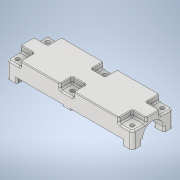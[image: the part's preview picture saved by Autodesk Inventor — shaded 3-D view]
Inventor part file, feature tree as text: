
AUTODESK INVENTOR PART (.ipt)
format: ipt  version: 2020 (Build 240168000, 168)  size: 884,736 bytes
history: native  units: mm
features: sketch x16, extrude x15, projected_geometry x10, other x4, fillet x3, boolean_combine x2, mirror x1
ambient origin geometry x8: Origin, YZ Plane, XZ Plane, XY Plane, X Axis, Y Axis, Z Axis, Center Point
bodies: Volumenkörper1 (feature_tree), Solid2 (feature_tree), Solid3 (feature_tree), Solid4 (feature_tree)
feature tree (51):
  other  "rolinho.ipt"
  extrude  "Extrusion1"  Depth=11.0mm
  other  "Spirale1"
  mirror  "Spiegeln1"
  extrude  "Extrusion5"  Depth=7.0mm
  extrude  "Extrusion6"  Depth=1.0mm
  boolean_combine  "Combine1"
  extrude  "Extrusion7"  Depth=10.0mm TaperAngle=0.0deg
  extrude  "Extrusion8"  Depth=7.0mm TaperAngle=0.0deg
  extrude  "Extrusion9"  Depth=24.0mm
  extrude  "Extrusion10"  Depth=12.0mm TaperAngle=0.0deg
  extrude  "Extrusion11"  Depth=4.0mm
  extrude  "Extrusion13"  Depth=20.0mm
  fillet  "Fillet2"  Radius=10.0mm
  fillet  "Fillet3"  Radius=77.15mm
  fillet  "Fillet4"  Radius=30.0mm
  extrude  "Extrusion14"  Depth=6.0mm
  extrude  "Extrusion15"  Depth=10.0mm TaperAngle=0.0deg
  extrude  "Extrusion16"  Depth=3.0mm
  extrude  "Extrusion17"  Depth=48.0mm
  extrude  "Extrusion19"  Depth=4.0mm
  extrude  "Extrusion20"  Depth=7.9mm
  boolean_combine  "Combine2"
  sketch  "Skizze1"  dims[d0=6.0mm d1=11.0mm]
  sketch  "Skizze3"  dims[d2=36.0mm d3=0.0mm]
  projected_geometry  "Projizierte Kontur2"
  sketch  "Sketch7"  dims[d8=7.0mm d9=24.5mm d10=10.0mm d11=0.0mm d12=90.0deg d13=90.0deg d14=0.0mm d15=0.0mm d16=4.0mm]
  sketch  "Sketch8"  dims[d17=13.962634mm d18=1.0mm]
  sketch  "Sketch9"  dims[d19=0.1mm d32=10.0mm d33=0.0mm]
  projected_geometry  "Projected Loop4"
  sketch  "Sketch10"  dims[d34=7.0mm d35=100.0mm d36=0.0mm]
  sketch  "Sketch11"  dims[d37=82.0mm d38=0.0mm d39=24.0mm]
  projected_geometry  "Projected Loop5"
  projected_geometry  "Projected Loop6"
  sketch  "Sketch12"  dims[d40=30.0mm d41=12.0mm d42=0.0mm]
  sketch  "Sketch13"  dims[d43=3.0mm d44=4.0mm]
  projected_geometry  "Projected Loop7"
  projected_geometry  "Projected Loop8"
  sketch  "Sketch15"  dims[d45=4.0mm d46=20.0mm d48=22.0mm d49=20.0mm d51=84.0mm d54=10.0mm d55=0.0mm d56=77.15mm d57=30.0mm]
  sketch  "Sketch16"  dims[d62=4.0mm d63=0.0mm d64=6.0mm]
  projected_geometry  "Projected Loop10"
  sketch  "Sketch17"  dims[d65=10.0mm d66=0.0mm d67=10.0mm d68=0.0mm]
  projected_geometry  "Projected Loop11"
  projected_geometry  "Projected Loop12"
  sketch  "Sketch18"  dims[d76=3.0mm d77=3.0mm]
  sketch  "Sketch19"  dims[d78=4.0mm d79=48.0mm]
  sketch  "Sketch21"  dims[d80=46.0mm d81=4.0mm]
  projected_geometry  "Projected Loop13"
  sketch  "Sketch22"  dims[d85=7.0mm d86=6.9mm d87=3.5mm d88=7.0mm d89=6.9mm d90=3.5mm d91=10.0mm d92=10.0mm d93=10.0mm d94=10.0mm d95=10.0mm d96=10.0mm d97=10.0mm d98=10.0mm d99=10.0mm d100=10.0mm d101=10.0mm d102=10.0mm d103=4.0mm d104=0.0mm d105=1.0mm d106=1.0mm d107=2.0mm d108=0.5mm d109=6.5mm d110=2.1mm d111=0.0mm d112=6.5mm d113=2.1mm d114=0.0mm d115=180.0deg d116=6.9mm d117=6.9mm d118=6.9mm d119=6.9mm d120=12.0mm d121=0.2mm d122=0.0mm d123=15.0mm d124=0.2mm d125=0.0mm d126=7.9mm d127=0.0mm d128=7.9mm d129=0.0mm d132=3.0mm d133=0.0mm d134=13.0mm d135=10.0mm d136=0.0mm d137=10.0mm]
  other  "Solid1::rolinho.ipt"
  other  "TaggingFeature1"
